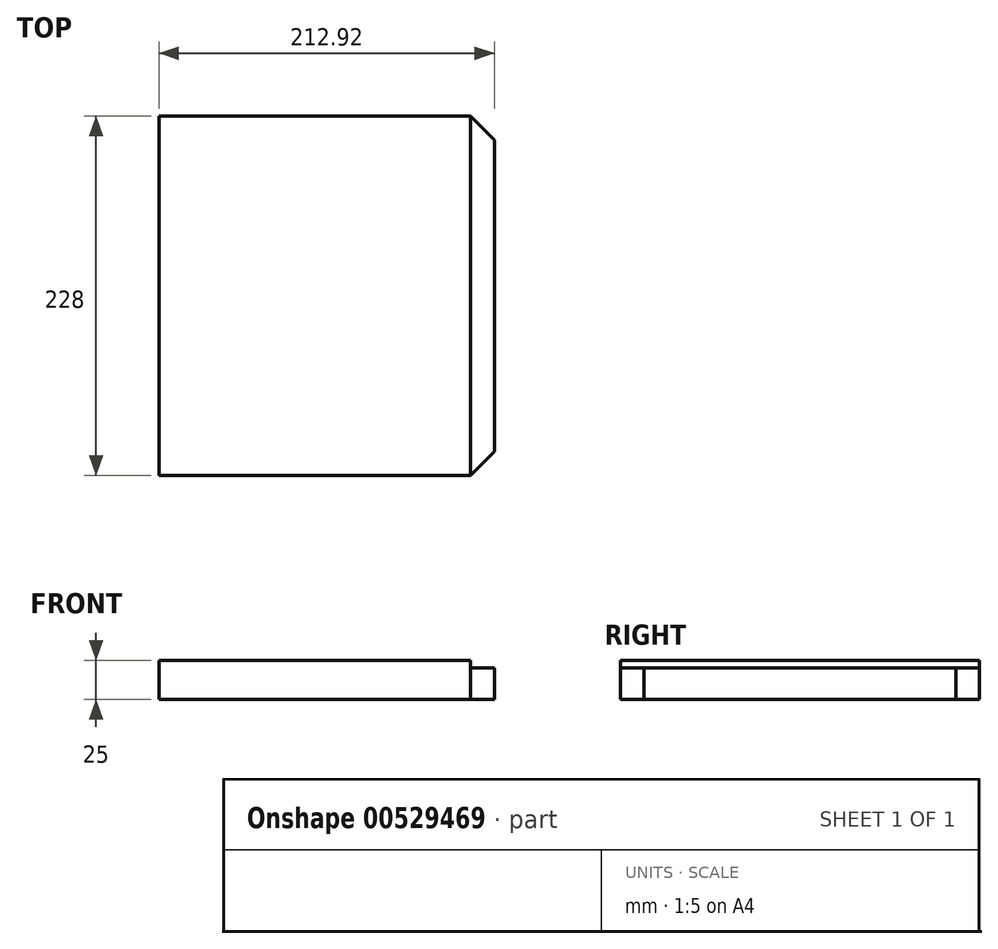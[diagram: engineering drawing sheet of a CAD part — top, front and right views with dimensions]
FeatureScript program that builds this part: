
annotation { "Feature Type Name" : "Feature", "Feature Type Description" : "" }
export const myFeature = defineFeature(function(context is Context, id is Id, definition is map)
    precondition{}
    {
        {
            var Q0;
            Q0=qCreatedBy(makeId("Top.planeOp"),FACE);
            var sketch = newSketch(context, id + "F0", { "sketchPlane" : qUnion([Q0])});
            skLineSegment(sketch, "E0.bottom", {"start": v(0, 0) * mm, "end": v(197.92, 0) * mm});
            skLineSegment(sketch, "E0.top", {"start": v(0, 228) * mm, "end": v(197.92, 228) * mm});
            skLineSegment(sketch, "E0.left", {"start": v(0, 0) * mm, "end": v(0, 228) * mm});
            skLineSegment(sketch, "E0.right", {"start": v(197.92, 0) * mm, "end": v(197.92, 228) * mm});
            skLineSegment(sketch, "E1", {"start": v(197.92, 228) * mm, "end": v(212.92, 213) * mm});
            skLineSegment(sketch, "E2", {"start": v(212.92, 213) * mm, "end": v(212.92, 15) * mm});
            skLineSegment(sketch, "E3", {"start": v(212.92, 15) * mm, "end": v(197.92, 0) * mm});
            skSolve(sketch);
        }
        {
            var Q0;
            Q0=makeQuery(id+"F0.imprint","IMPRINT",FACE,{"disambiguationData":[TD([[makeQuery(id+"F0.imprint","IMPRINT",EDGE,{"derivedFrom":sQuery(id+"F0.wireOp",EDGE,"E0.bottom")}),1.0]])]});
            extrude(context, id + "F1", {"entities" : qUnion([Q0]), "depth" : 25 * mm, "offsetDistance" : 25 * mm});
        }
        {
            var Q0;
            Q0=makeQuery(id+"F0.imprint","IMPRINT",FACE,{"disambiguationData":[TD([[makeQuery(id+"F0.imprint","IMPRINT",EDGE,{"derivedFrom":sQuery(id+"F0.wireOp",EDGE,"E0.right")}),-1.0]])]});
            extrude(context, id + "F2", {"entities" : qUnion([Q0]), "operationType" : NewBodyOperationType.ADD, "depth" : 20 * mm, "offsetDistance" : 25 * mm});
        }
    });
